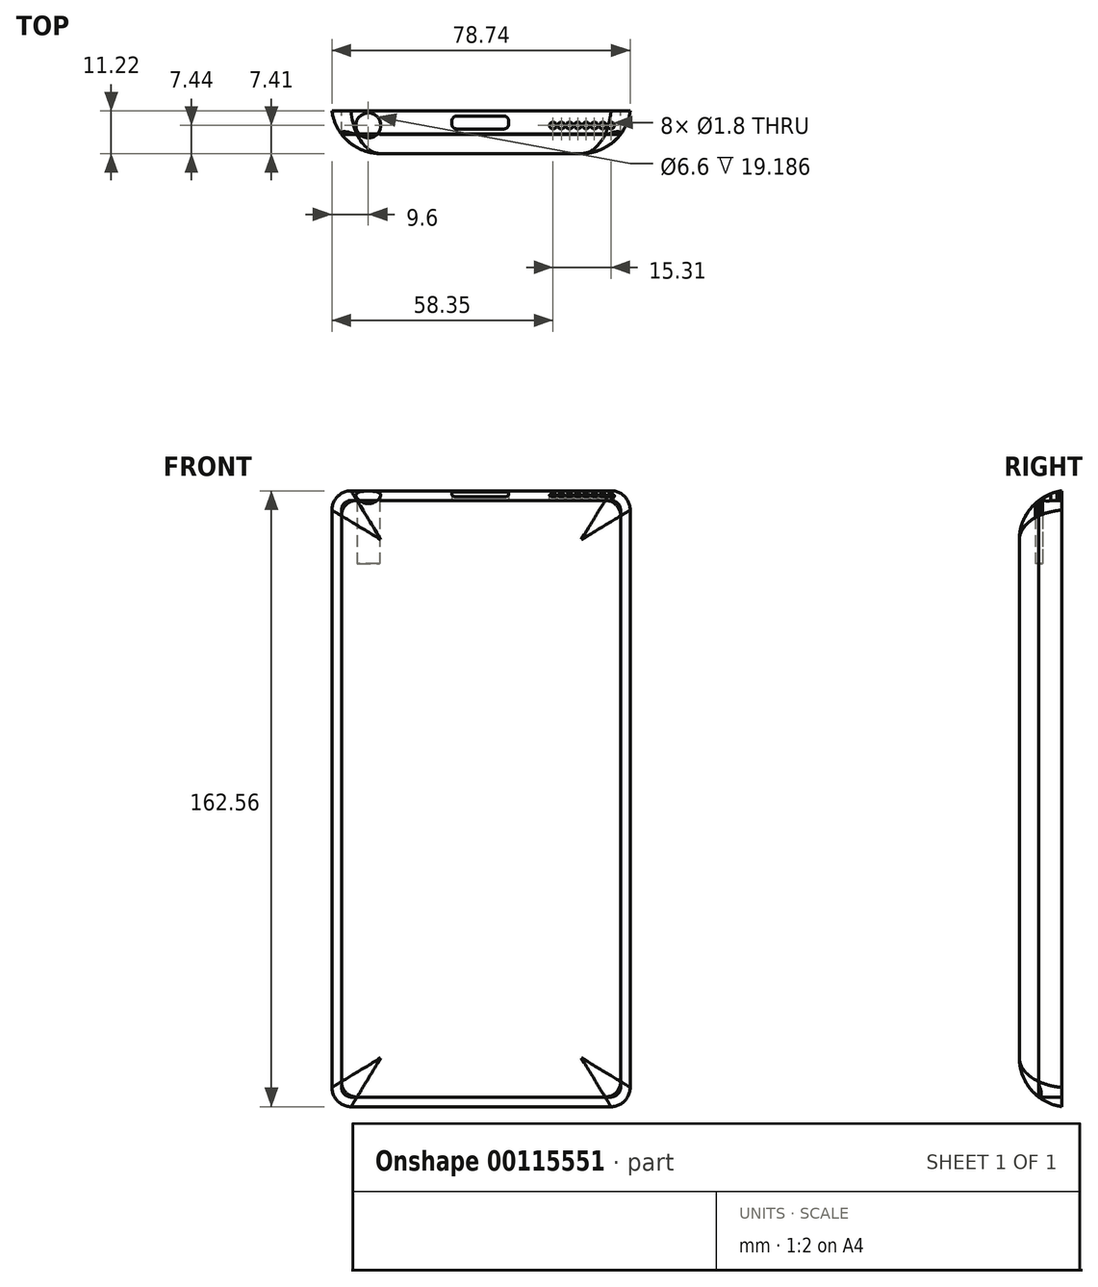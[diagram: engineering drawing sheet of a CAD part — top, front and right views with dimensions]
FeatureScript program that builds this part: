
annotation { "Feature Type Name" : "Feature", "Feature Type Description" : "" }
export const myFeature = defineFeature(function(context is Context, id is Id, definition is map)
    precondition{}
    {
        {
            var Q0;
            Q0=qCreatedBy(makeId("Front.planeOp"),FACE);
            var sketch = newSketch(context, id + "F0", { "sketchPlane" : qUnion([Q0])});
            skLineSegment(sketch, "E0.bottom", {"start": v(-39.09, 85.86) * mm, "end": v(39.65, 85.86) * mm});
            skLineSegment(sketch, "E0.top", {"start": v(-39.09, -76.7) * mm, "end": v(39.65, -76.7) * mm});
            skLineSegment(sketch, "E0.left", {"start": v(-39.09, 85.86) * mm, "end": v(-39.09, -76.7) * mm});
            skLineSegment(sketch, "E0.right", {"start": v(39.65, 85.86) * mm, "end": v(39.65, -76.7) * mm});
            skSolve(sketch);
        }
        {
            var Q0;
            Q0 = qSketchRegion(id + "F0", true);
            extrude(context, id + "F1", {"entities" : qUnion([Q0]), "depth" : 7.62 * mm});
        }
        {
            var Q0;
            Q0=makeQuery(id+"F1.opExtrude","SWEPT_EDGE",EDGE,{"disambiguationData":[OSD([sQuery(id+"F0.wireOp",EDGE,"E0.bottom"),sQuery(id+"F0.wireOp",EDGE,"E0.left")])]});
            var Q1;
            Q1=makeQuery(id+"F1.opExtrude","SWEPT_EDGE",EDGE,{"disambiguationData":[OSD([sQuery(id+"F0.wireOp",EDGE,"E0.bottom"),sQuery(id+"F0.wireOp",EDGE,"E0.right")])]});
            var Q2;
            Q2=makeQuery(id+"F1.opExtrude","SWEPT_EDGE",EDGE,{"disambiguationData":[OSD([sQuery(id+"F0.wireOp",EDGE,"E0.top"),sQuery(id+"F0.wireOp",EDGE,"E0.right")])]});
            var Q3;
            Q3=makeQuery(id+"F1.opExtrude","SWEPT_EDGE",EDGE,{"disambiguationData":[OSD([sQuery(id+"F0.wireOp",EDGE,"E0.top"),sQuery(id+"F0.wireOp",EDGE,"E0.left")])]});
            fillet(context, id + "F2", {"entities" : qUnion([Q0, Q1, Q2, Q3]), "radius" : 5.08 * mm, "tangentPropagation" : true, "allowEdgeOverflow" : false});
        }
        {
            var Q0;
            Q0=makeQuery(id+"F1.opExtrude","CAP_FACE",FACE,{"disambiguationData":[OSD([sQuery(id+"F0.wireOp",EDGE,"E0.bottom"),sQuery(id+"F0.wireOp",EDGE,"E0.top"),sQuery(id+"F0.wireOp",EDGE,"E0.left"),sQuery(id+"F0.wireOp",EDGE,"E0.right")])],"isStart":true});
            shell(context, id + "F3", {"entities" : qUnion([Q0]), "thickness" : 2.54 * mm});
        }
        {
            var Q0;
            Q0=qCreatedBy(makeId("Top.planeOp"),FACE);
            var sketch = newSketch(context, id + "F4", { "sketchPlane" : qUnion([Q0])});
            skLineSegment(sketch, "E1.bottom", {"start": v(-7.43, -4.71) * mm, "end": v(7.56, -4.71) * mm});
            skLineSegment(sketch, "E1.top", {"start": v(-7.43, -1.31) * mm, "end": v(7.56, -1.31) * mm});
            skLineSegment(sketch, "E1.left", {"start": v(-7.43, -4.71) * mm, "end": v(-7.43, -1.31) * mm});
            skLineSegment(sketch, "E1.right", {"start": v(7.56, -4.71) * mm, "end": v(7.56, -1.31) * mm});
            skSolve(sketch);
        }
        {
            var Q0;
            Q0 = qSketchRegion(id + "F4", true);
            extrude(context, id + "F5", {"entities" : qUnion([Q0]), "operationType" : NewBodyOperationType.REMOVE, "depth" : 115.78 * mm});
        }
        {
            var Q0;
            Q0=makeQuery(id+"F5.boolean.opBoolean","COPY",EDGE,{"derivedFrom":makeQuery(id+"F5.opExtrude","SWEPT_EDGE",EDGE,{"disambiguationData":[OSD([sQuery(id+"F4.wireOp",EDGE,"E1.bottom"),sQuery(id+"F4.wireOp",EDGE,"E1.left")])]})});
            var Q1;
            Q1=makeQuery(id+"F5.boolean.opBoolean","COPY",EDGE,{"derivedFrom":makeQuery(id+"F5.opExtrude","SWEPT_EDGE",EDGE,{"disambiguationData":[OSD([sQuery(id+"F4.wireOp",EDGE,"E1.bottom"),sQuery(id+"F4.wireOp",EDGE,"E1.right")])]})});
            var Q2;
            Q2=makeQuery(id+"F5.boolean.opBoolean","COPY",EDGE,{"derivedFrom":makeQuery(id+"F5.opExtrude","SWEPT_EDGE",EDGE,{"disambiguationData":[OSD([sQuery(id+"F4.wireOp",EDGE,"E1.top"),sQuery(id+"F4.wireOp",EDGE,"E1.right")])]})});
            var Q3;
            Q3=makeQuery(id+"F5.boolean.opBoolean","COPY",EDGE,{"derivedFrom":makeQuery(id+"F5.opExtrude","SWEPT_EDGE",EDGE,{"disambiguationData":[OSD([sQuery(id+"F4.wireOp",EDGE,"E1.top"),sQuery(id+"F4.wireOp",EDGE,"E1.left")])]})});
            fillet(context, id + "F6", {"entities" : qUnion([Q0, Q1, Q2, Q3]), "radius" : 1.27 * mm, "tangentPropagation" : true, "allowEdgeOverflow" : false});
        }
        {
            var Q0;
            Q0=makeQuery(id+"F1.opExtrude","SWEPT_FACE",FACE,{"disambiguationData":[OSD([sQuery(id+"F0.wireOp",EDGE,"E0.bottom")])]});
            var sketch = newSketch(context, id + "F7", { "sketchPlane" : qUnion([Q0])});
            skCircle(sketch, "E2", {"center": v(34.57, -3.81) * mm, "radius": 0.9 * mm});
            skCircle(sketch, "E3", {"center": v(32.38, -3.81) * mm, "radius": 0.9 * mm});
            skCircle(sketch, "E4", {"center": v(30.2, -3.81) * mm, "radius": 0.9 * mm});
            skCircle(sketch, "E5", {"center": v(28, -3.81) * mm, "radius": 0.9 * mm});
            skCircle(sketch, "E6", {"center": v(25.82, -3.81) * mm, "radius": 0.9 * mm});
            skLineSegment(sketch, "E7", {"start": v(34.57, -3.81) * mm, "end": v(21.45, -3.81) * mm});
            skCircle(sketch, "E8", {"center": v(23.63, -3.81) * mm, "radius": 0.9 * mm});
            skCircle(sketch, "E9", {"center": v(21.45, -3.81) * mm, "radius": 0.9 * mm});
            skCircle(sketch, "E10", {"center": v(19.26, -3.81) * mm, "radius": 0.9 * mm});
            skLineSegment(sketch, "E11", {"start": v(21.45, -3.81) * mm, "end": v(19.26, -3.81) * mm});
            skSolve(sketch);
        }
        {
            var Q0;
            Q0 = qSketchRegion(id + "F7", true);
            extrude(context, id + "F8", {"entities" : qUnion([Q0]), "operationType" : NewBodyOperationType.REMOVE, "oppositeDirection" : true, "depth" : 36.9 * mm});
        }
        {
            var Q0;
            Q0=makeQuery(id+"F1.opExtrude","CAP_FACE",FACE,{"disambiguationData":[OSD([sQuery(id+"F0.wireOp",EDGE,"E0.bottom"),sQuery(id+"F0.wireOp",EDGE,"E0.top"),sQuery(id+"F0.wireOp",EDGE,"E0.left"),sQuery(id+"F0.wireOp",EDGE,"E0.right")])],"isStart":false});
            extrude(context, id + "F9", {"entities" : qUnion([Q0]), "operationType" : NewBodyOperationType.ADD, "depth" : 3.6 * mm});
        }
        {
            var Q0;
            Q0=qCreatedBy(makeId("Top.planeOp"),FACE);
            var sketch = newSketch(context, id + "F10", { "sketchPlane" : qUnion([Q0])});
            skLineSegment(sketch, "E12", {"start": v(-39.13, 0) * mm, "end": v(-39.13, -9.45) * mm});
            skCircle(sketch, "E13", {"center": v(-29.49, -3.78) * mm, "radius": 3.3 * mm});
            skSolve(sketch);
        }
        {
            var Q0;
            Q0 = qSketchRegion(id + "F10", true);
            extrude(context, id + "F11", {"entities" : qUnion([Q0]), "operationType" : NewBodyOperationType.REMOVE, "depth" : 103.1 * mm, "hasSecondDirection" : true, "secondDirectionOppositeDirection" : false, "secondDirectionDepth" : 66.6 * mm});
        }
        {
            var Q0;
            Q0=makeQuery(id+"F9.opExtrude","CAP_EDGE",EDGE,{"disambiguationData":[OSD([sQuery(id+"F0.wireOp",EDGE,"E0.top")])],"isStart":false});
            fillet(context, id + "F12", {"entities" : qUnion([Q0]), "radius" : 13.02 * mm, "tangentPropagation" : true, "allowEdgeOverflow" : false});
        }
        {
            var Q0;
            Q0=makeQuery(id+"F3.opShell","OFFSET_FACE",FACE,{"disambiguationData":[OSD([sQuery(id+"F0.wireOp",EDGE,"E0.bottom"),sQuery(id+"F0.wireOp",EDGE,"E0.top"),sQuery(id+"F0.wireOp",EDGE,"E0.left"),sQuery(id+"F0.wireOp",EDGE,"E0.right")])]});
            extrude(context, id + "F13", {"entities" : qUnion([Q0]), "operationType" : NewBodyOperationType.REMOVE, "depth" : 0.3 * mm});
        }
        {
            var Q0;
            Q0=makeQuery(id+"F3.opShell","OFFSET_FACE",FACE,{"disambiguationData":[OSD([sQuery(id+"F0.wireOp",EDGE,"E0.bottom"),sQuery(id+"F0.wireOp",EDGE,"E0.top"),sQuery(id+"F0.wireOp",EDGE,"E0.left"),sQuery(id+"F0.wireOp",EDGE,"E0.right")])]});
            extrude(context, id + "F14", {"entities" : qUnion([Q0]), "operationType" : NewBodyOperationType.REMOVE, "oppositeDirection" : true, "depth" : 1.02 * mm});
        }
    });
